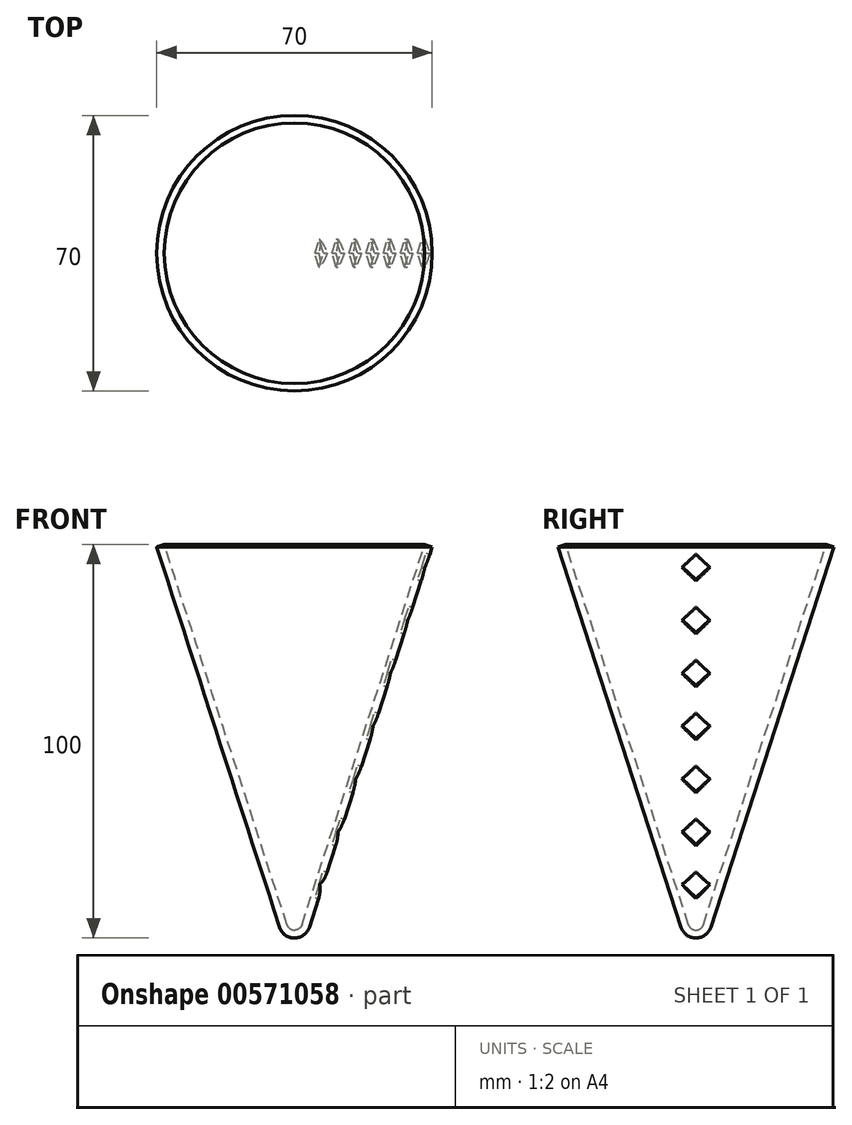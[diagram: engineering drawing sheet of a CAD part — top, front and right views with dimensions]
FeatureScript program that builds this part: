
annotation { "Feature Type Name" : "Feature", "Feature Type Description" : "" }
export const myFeature = defineFeature(function(context is Context, id is Id, definition is map)
    precondition{}
    {
        {
            var Q0;
            Q0=qCreatedBy(makeId("Front.planeOp"),FACE);
            var sketch = newSketch(context, id + "F0", { "sketchPlane" : qUnion([Q0])});
            skLineSegment(sketch, "E0", {"start": v(0, 9.02) * mm, "end": v(0, 11.02) * mm});
            skArc(sketch, "E1", {"start": v(0, 9.02) * mm, "mid": v(2.35, 9.78) * mm, "end": v(3.8, 11.79) * mm});
            skLineSegment(sketch, "E2", {"start": v(3.8, 11.79) * mm, "end": v(35, 108.4) * mm});
            skLineSegment(sketch, "E3", {"start": v(35, 108.4) * mm, "end": v(33.1, 109.02) * mm});
            skLineSegment(sketch, "E4", {"start": v(33.1, 109.02) * mm, "end": v(1.9, 12.4) * mm});
            skArc(sketch, "E5", {"start": v(0, 11.02) * mm, "mid": v(1.18, 11.4) * mm, "end": v(1.9, 12.4) * mm});
            skSolve(sketch);
        }
        {
            var Q0;
            Q0 = qSketchRegion(id + "F0", true);
            var Q1;
            Q1=sQuery(id+"F0.wireOp",EDGE,"E0");
            revolve(context, id + "F1", {"entities" : qUnion([Q0]), "axis" : qUnion([Q1]), "revolveType" : RevolveType.FULL});
        }
        {
            var Q0;
            Q0=sQuery(id+"F0.wireOp",EDGE,"E2");
            cPlane(context, id + "F2", {"entities" : qUnion([Q0]), "cplaneType" : CPlaneType.LINE_ANGLE, "offset" : 25 * mm, "angle" : 0 * degree, "width" : 150 * mm, "height" : 150 * mm});
        }
        {
            var Q0;
            Q0=qCreatedBy(id+"F2.planeOp",FACE);
            var sketch = newSketch(context, id + "F3", { "sketchPlane" : qUnion([Q0])});
            skLineSegment(sketch, "E6.bottom", {"start": v(-3.54, 108.38) * mm, "end": v(0, 111.91) * mm});
            skLineSegment(sketch, "E6.top", {"start": v(0, 104.84) * mm, "end": v(3.54, 108.38) * mm});
            skLineSegment(sketch, "E6.left", {"start": v(-3.54, 108.38) * mm, "end": v(0, 104.84) * mm});
            skLineSegment(sketch, "E6.right", {"start": v(0, 111.91) * mm, "end": v(3.54, 108.38) * mm});
            skLineSegment(sketch, "E7.1.0.0", {"start": v(-3.54, 94.24) * mm, "end": v(0, 97.77) * mm});
            skLineSegment(sketch, "E7.1.0.1", {"start": v(0, 97.77) * mm, "end": v(3.54, 94.24) * mm});
            skLineSegment(sketch, "E7.1.0.2", {"start": v(0, 90.7) * mm, "end": v(3.54, 94.24) * mm});
            skLineSegment(sketch, "E7.1.0.3", {"start": v(-3.54, 94.24) * mm, "end": v(0, 90.7) * mm});
            skLineSegment(sketch, "E7.2.0.0", {"start": v(-3.54, 80.1) * mm, "end": v(0, 83.63) * mm});
            skLineSegment(sketch, "E7.2.0.1", {"start": v(0, 83.63) * mm, "end": v(3.54, 80.1) * mm});
            skLineSegment(sketch, "E7.2.0.2", {"start": v(0, 76.56) * mm, "end": v(3.54, 80.1) * mm});
            skLineSegment(sketch, "E7.2.0.3", {"start": v(-3.54, 80.1) * mm, "end": v(0, 76.56) * mm});
            skLineSegment(sketch, "E7.direction1", {"start": v(0, 111.91) * mm, "end": v(0, 97.77) * mm, "construction": true});
            skLineSegment(sketch, "E8.0.3.0", {"start": v(-3.54, 65.95) * mm, "end": v(0, 69.49) * mm});
            skLineSegment(sketch, "E8.3.3.0", {"start": v(0, 69.49) * mm, "end": v(3.54, 65.95) * mm});
            skLineSegment(sketch, "E8.6.3.0", {"start": v(0, 62.42) * mm, "end": v(3.54, 65.95) * mm});
            skLineSegment(sketch, "E8.9.3.0", {"start": v(-3.54, 65.95) * mm, "end": v(0, 62.42) * mm});
            skLineSegment(sketch, "E8.0.4.0", {"start": v(-3.54, 51.81) * mm, "end": v(0, 55.35) * mm});
            skLineSegment(sketch, "E8.3.4.0", {"start": v(0, 55.35) * mm, "end": v(3.54, 51.81) * mm});
            skLineSegment(sketch, "E8.6.4.0", {"start": v(0, 48.27) * mm, "end": v(3.54, 51.81) * mm});
            skLineSegment(sketch, "E8.9.4.0", {"start": v(-3.54, 51.81) * mm, "end": v(0, 48.27) * mm});
            skLineSegment(sketch, "E9", {"start": v(0, 90.7) * mm, "end": v(0, 83.63) * mm, "construction": true});
            skLineSegment(sketch, "E10", {"start": v(0, 69.49) * mm, "end": v(0, 62.42) * mm, "construction": true});
            skLineSegment(sketch, "E11.0.5.0", {"start": v(-3.54, 37.67) * mm, "end": v(0, 41.2) * mm});
            skLineSegment(sketch, "E11.3.5.0", {"start": v(0, 41.2) * mm, "end": v(3.54, 37.67) * mm});
            skLineSegment(sketch, "E11.6.5.0", {"start": v(0, 34.13) * mm, "end": v(3.54, 37.67) * mm});
            skLineSegment(sketch, "E11.9.5.0", {"start": v(-3.54, 37.67) * mm, "end": v(0, 34.13) * mm});
            skLineSegment(sketch, "E11.0.6.0", {"start": v(-3.54, 23.53) * mm, "end": v(0, 27.06) * mm});
            skLineSegment(sketch, "E11.3.6.0", {"start": v(0, 27.06) * mm, "end": v(3.54, 23.53) * mm});
            skLineSegment(sketch, "E11.6.6.0", {"start": v(0, 20) * mm, "end": v(3.54, 23.53) * mm});
            skLineSegment(sketch, "E11.9.6.0", {"start": v(-3.54, 23.53) * mm, "end": v(0, 20) * mm});
            skSolve(sketch);
        }
        {
            var Q0;
            Q0 = qSketchRegion(id + "F3", true);
            extrude(context, id + "F4", {"entities" : qUnion([Q0]), "operationType" : NewBodyOperationType.REMOVE, "oppositeDirection" : true, "depth" : 1 * mm, "offsetDistance" : 25 * mm});
        }
    });
